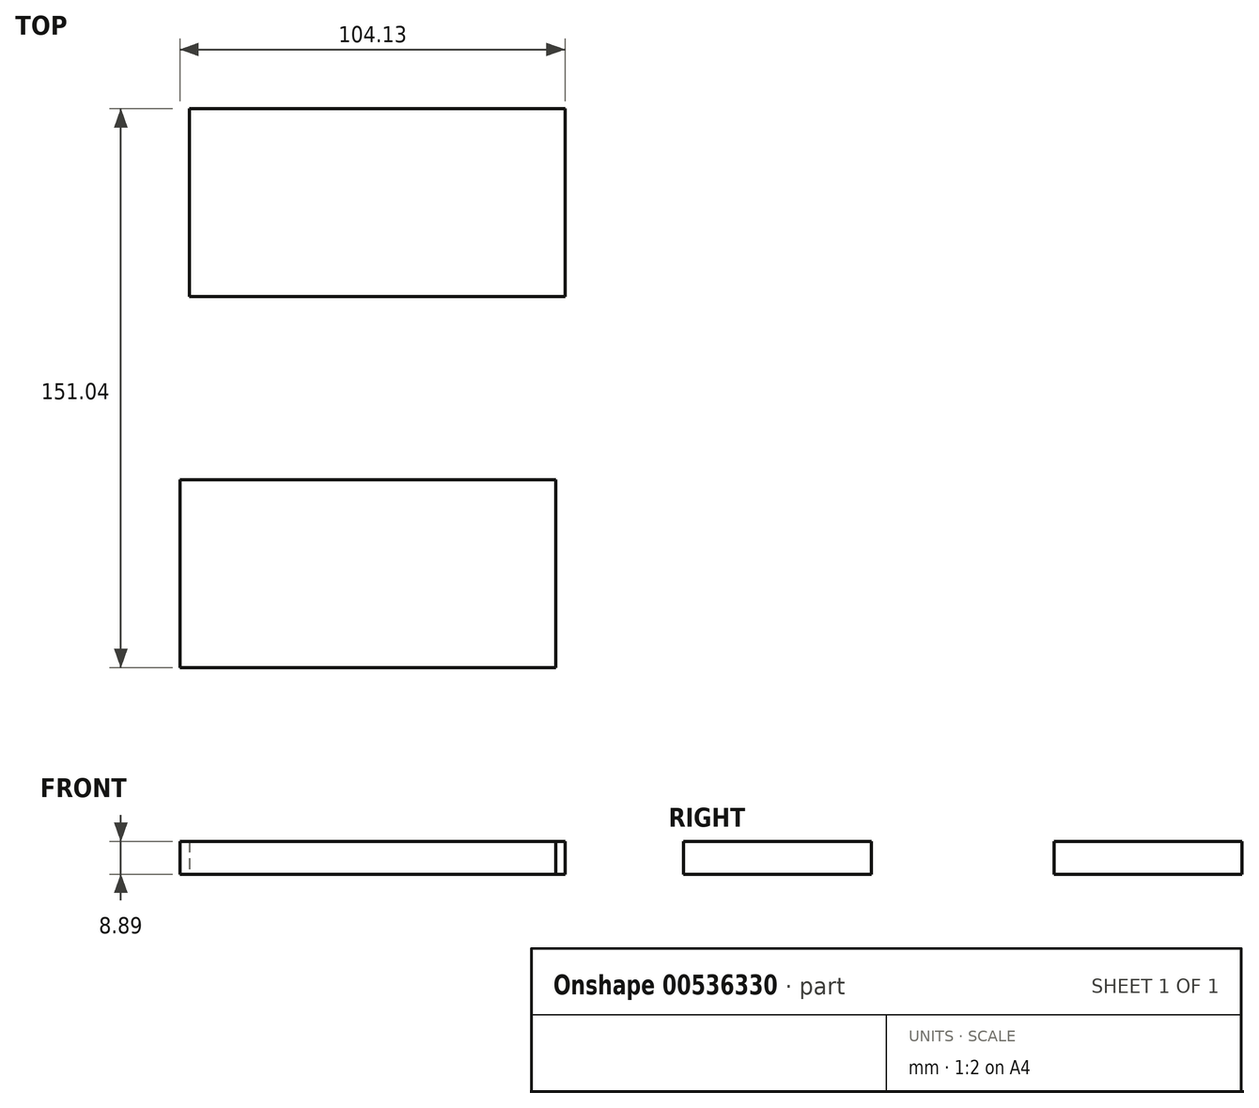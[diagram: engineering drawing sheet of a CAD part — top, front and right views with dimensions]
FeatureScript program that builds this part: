
annotation { "Feature Type Name" : "Feature", "Feature Type Description" : "" }
export const myFeature = defineFeature(function(context is Context, id is Id, definition is map)
    precondition{}
    {
        {
            var Q0;
            Q0=qCreatedBy(makeId("Top.planeOp"),FACE);
            var sketch = newSketch(context, id + "F0", { "sketchPlane" : qUnion([Q0])});
            skLineSegment(sketch, "E0.bottom", {"start": v(-51.44, 100.24) * mm, "end": v(50.16, 100.24) * mm});
            skLineSegment(sketch, "E0.top", {"start": v(-51.44, 49.44) * mm, "end": v(50.16, 49.44) * mm});
            skLineSegment(sketch, "E0.left", {"start": v(-51.44, 100.24) * mm, "end": v(-51.44, 49.44) * mm});
            skLineSegment(sketch, "E0.right", {"start": v(50.16, 100.24) * mm, "end": v(50.16, 49.44) * mm});
            skLineSegment(sketch, "E1.bottom", {"start": v(-53.97, 0) * mm, "end": v(47.63, 0) * mm});
            skLineSegment(sketch, "E1.top", {"start": v(-53.97, -50.8) * mm, "end": v(47.63, -50.8) * mm});
            skLineSegment(sketch, "E1.left", {"start": v(-53.97, 0) * mm, "end": v(-53.97, -50.8) * mm});
            skLineSegment(sketch, "E1.right", {"start": v(47.63, 0) * mm, "end": v(47.63, -50.8) * mm});
            skSolve(sketch);
        }
        {
            var Q0;
            Q0=makeQuery(id+"F0.imprint","IMPRINT",FACE,{"disambiguationData":[TD([[makeQuery(id+"F0.imprint","IMPRINT",EDGE,{"derivedFrom":sQuery(id+"F0.wireOp",EDGE,"E0.bottom")}),-1.0]])]});
            var Q1;
            Q1=makeQuery(id+"F0.imprint","IMPRINT",FACE,{"disambiguationData":[TD([[makeQuery(id+"F0.imprint","IMPRINT",EDGE,{"derivedFrom":sQuery(id+"F0.wireOp",EDGE,"E1.bottom")}),-1.0]])]});
            extrude(context, id + "F1", {"entities" : qUnion([Q0, Q1]), "depth" : 8.9 * mm, "offsetDistance" : 25.4 * mm});
        }
    });
